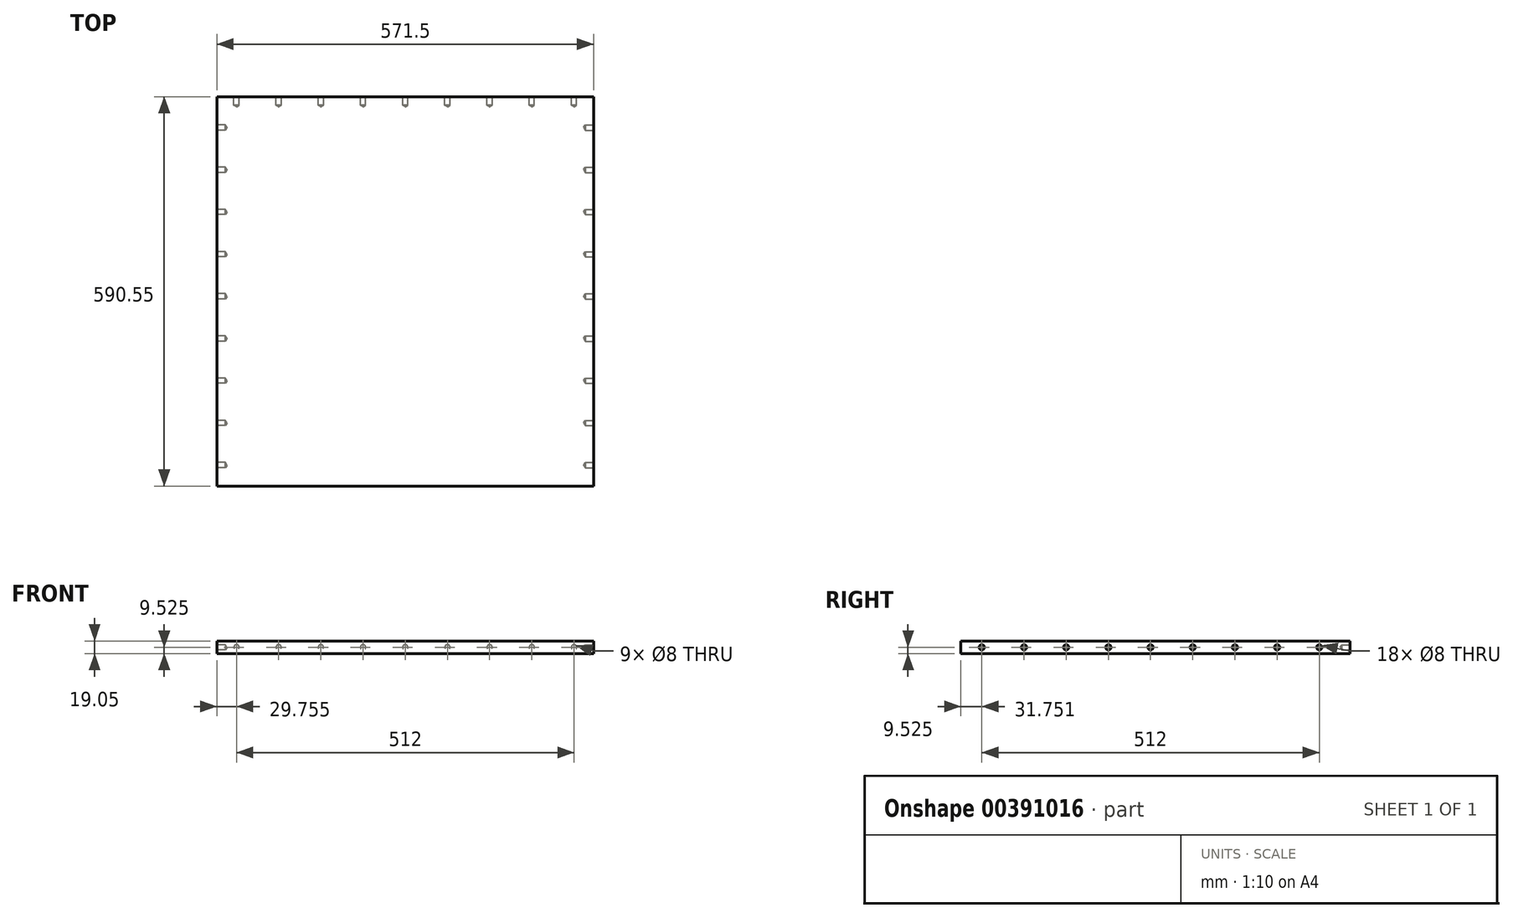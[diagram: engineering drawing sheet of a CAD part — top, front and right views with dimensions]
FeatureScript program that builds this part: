
annotation { "Feature Type Name" : "Feature", "Feature Type Description" : "" }
export const myFeature = defineFeature(function(context is Context, id is Id, definition is map)
    precondition{}
    {
        {
            var Q0;
            Q0=qCreatedBy(makeId("Top.planeOp"),FACE);
            var sketch = newSketch(context, id + "F0", { "sketchPlane" : qUnion([Q0])});
            skLineSegment(sketch, "E0.bottom", {"start": v(-308.17, 303.25) * mm, "end": v(263.33, 303.25) * mm});
            skLineSegment(sketch, "E0.top", {"start": v(-308.17, -287.3) * mm, "end": v(263.33, -287.3) * mm});
            skLineSegment(sketch, "E0.left", {"start": v(-308.17, 303.25) * mm, "end": v(-308.17, -287.3) * mm});
            skLineSegment(sketch, "E0.right", {"start": v(263.33, 303.25) * mm, "end": v(263.33, -287.3) * mm});
            skSolve(sketch);
        }
        {
            var Q0;
            Q0=makeQuery(id+"F0.imprint","IMPRINT",FACE,{"disambiguationData":[TD([[makeQuery(id+"F0.imprint","IMPRINT",EDGE,{"derivedFrom":sQuery(id+"F0.wireOp",EDGE,"E0.bottom")}),-1.0]])]});
            extrude(context, id + "F1", {"entities" : qUnion([Q0]), "depth" : 19.05 * mm});
        }
        {
            var Q0;
            Q0=makeQuery(id+"F1.opExtrude","SWEPT_FACE",FACE,{"disambiguationData":[OSD([sQuery(id+"F0.wireOp",EDGE,"E0.right")])]});
            var sketch = newSketch(context, id + "F2", { "sketchPlane" : qUnion([Q0])});
            skCircle(sketch, "E1", {"center": v(-255.55, 9.53) * mm, "radius": 4 * mm});
            skCircle(sketch, "E2.1.0.0", {"center": v(-191.55, 9.53) * mm, "radius": 4 * mm});
            skCircle(sketch, "E2.2.0.0", {"center": v(-127.55, 9.53) * mm, "radius": 4 * mm});
            skCircle(sketch, "E2.3.0.0", {"center": v(-63.55, 9.53) * mm, "radius": 4 * mm});
            skCircle(sketch, "E2.4.0.0", {"center": v(0.45, 9.53) * mm, "radius": 4 * mm});
            skCircle(sketch, "E2.5.0.0", {"center": v(64.45, 9.53) * mm, "radius": 4 * mm});
            skCircle(sketch, "E2.6.0.0", {"center": v(128.45, 9.53) * mm, "radius": 4 * mm});
            skCircle(sketch, "E2.7.0.0", {"center": v(192.45, 9.53) * mm, "radius": 4 * mm});
            skCircle(sketch, "E2.8.0.0", {"center": v(256.45, 9.53) * mm, "radius": 4 * mm});
            skLineSegment(sketch, "E2.direction1", {"start": v(-255.55, 9.53) * mm, "end": v(-191.55, 9.53) * mm, "construction": true});
            skSolve(sketch);
        }
        {
            var Q0;
            Q0=sQuery(id+"F2.wireOp",VERTEX,"E2.direction1.start");
            var Q1;
            Q1=sQuery(id+"F2.wireOp",VERTEX,"E2.1.0.0.center");
            var Q2;
            Q2=sQuery(id+"F2.wireOp",VERTEX,"E2.2.0.0.center");
            var Q3;
            Q3=sQuery(id+"F2.wireOp",VERTEX,"E2.3.0.0.center");
            var Q4;
            Q4=sQuery(id+"F2.wireOp",VERTEX,"E2.4.0.0.center");
            var Q5;
            Q5=sQuery(id+"F2.wireOp",VERTEX,"E2.5.0.0.center");
            var Q6;
            Q6=sQuery(id+"F2.wireOp",VERTEX,"E2.6.0.0.center");
            var Q7;
            Q7=sQuery(id+"F2.wireOp",VERTEX,"E2.7.0.0.center");
            var Q8;
            Q8=sQuery(id+"F2.wireOp",VERTEX,"E2.8.0.0.center");
            var Q9;
            Q9=makeQuery(id+"F1.opExtrude","SWEPT_BODY",BODY,{"disambiguationData":[OSD([sQuery(id+"F0.wireOp",EDGE,"E0.bottom"),sQuery(id+"F0.wireOp",EDGE,"E0.top"),sQuery(id+"F0.wireOp",EDGE,"E0.left"),sQuery(id+"F0.wireOp",EDGE,"E0.right")])]});
            hole(context, id + "F3", {"style" : HoleStyle.SIMPLE, "endStyle" : HoleEndStyle.BLIND, "standardTappedOrClearance" : lookupTablePath({ "standard" : "ISO", "size" : "8", "type" : "Drilled" }), "standardBlindInLast" : lookupTablePath({ "standard" : "ISO", "size" : "8", "type" : "Drilled" }), "holeDiameter" : 8 * mm, "holeDepth" : 12.7 * mm, "isTappedThrough" : true, "tappedDepth" : 12.7 * mm, "tapClearance" : 3, "startFromSketch" : true, "locations" : qUnion([Q0, Q1, Q2, Q3, Q4, Q5, Q6, Q7, Q8]), "scope" : qUnion([Q9])});
        }
        {
            var Q0;
            Q0=makeQuery(id+"F1.opExtrude","SWEPT_FACE",FACE,{"disambiguationData":[OSD([sQuery(id+"F0.wireOp",EDGE,"E0.left")])]});
            var sketch = newSketch(context, id + "F4", { "sketchPlane" : qUnion([Q0])});
            skCircle(sketch, "E3", {"center": v(255.55, 9.53) * mm, "radius": 4 * mm});
            skCircle(sketch, "E4.1.0.0", {"center": v(191.55, 9.53) * mm, "radius": 4 * mm});
            skCircle(sketch, "E4.2.0.0", {"center": v(127.55, 9.53) * mm, "radius": 4 * mm});
            skCircle(sketch, "E4.3.0.0", {"center": v(63.55, 9.53) * mm, "radius": 4 * mm});
            skCircle(sketch, "E4.4.0.0", {"center": v(-0.45, 9.53) * mm, "radius": 4 * mm});
            skCircle(sketch, "E4.5.0.0", {"center": v(-64.45, 9.53) * mm, "radius": 4 * mm});
            skCircle(sketch, "E4.6.0.0", {"center": v(-128.45, 9.53) * mm, "radius": 4 * mm});
            skCircle(sketch, "E4.7.0.0", {"center": v(-192.45, 9.53) * mm, "radius": 4 * mm});
            skCircle(sketch, "E4.8.0.0", {"center": v(-256.45, 9.53) * mm, "radius": 4 * mm});
            skLineSegment(sketch, "E4.direction1", {"start": v(255.55, 9.53) * mm, "end": v(191.55, 9.53) * mm, "construction": true});
            skSolve(sketch);
        }
        {
            var Q0;
            Q0=sQuery(id+"F4.wireOp",VERTEX,"E3.center");
            var Q1;
            Q1=sQuery(id+"F4.wireOp",VERTEX,"E4.direction1.end");
            var Q2;
            Q2=sQuery(id+"F4.wireOp",VERTEX,"E4.2.0.0.center");
            var Q3;
            Q3=sQuery(id+"F4.wireOp",VERTEX,"E4.3.0.0.center");
            var Q4;
            Q4=sQuery(id+"F4.wireOp",VERTEX,"E4.5.0.0.center");
            var Q5;
            Q5=sQuery(id+"F4.wireOp",VERTEX,"E4.4.0.0.center");
            var Q6;
            Q6=sQuery(id+"F4.wireOp",VERTEX,"E4.6.0.0.center");
            var Q7;
            Q7=sQuery(id+"F4.wireOp",VERTEX,"E4.7.0.0.center");
            var Q8;
            Q8=sQuery(id+"F4.wireOp",VERTEX,"E4.8.0.0.center");
            var Q9;
            Q9=makeQuery(id+"F1.opExtrude","SWEPT_BODY",BODY,{"disambiguationData":[OSD([sQuery(id+"F0.wireOp",EDGE,"E0.bottom"),sQuery(id+"F0.wireOp",EDGE,"E0.top"),sQuery(id+"F0.wireOp",EDGE,"E0.left"),sQuery(id+"F0.wireOp",EDGE,"E0.right")])]});
            hole(context, id + "F5", {"style" : HoleStyle.SIMPLE, "endStyle" : HoleEndStyle.BLIND, "standardTappedOrClearance" : lookupTablePath({ "standard" : "ISO", "size" : "8", "type" : "Drilled" }), "standardBlindInLast" : lookupTablePath({ "standard" : "ISO", "size" : "8", "type" : "Drilled" }), "holeDiameter" : 8 * mm, "holeDepth" : 12.7 * mm, "isTappedThrough" : true, "tappedDepth" : 12.7 * mm, "tapClearance" : 3, "startFromSketch" : true, "locations" : qUnion([Q0, Q1, Q2, Q3, Q4, Q5, Q6, Q7, Q8]), "scope" : qUnion([Q9])});
        }
        {
            var Q0;
            Q0=makeQuery(id+"F1.opExtrude","SWEPT_FACE",FACE,{"disambiguationData":[OSD([sQuery(id+"F0.wireOp",EDGE,"E0.bottom")])]});
            var sketch = newSketch(context, id + "F6", { "sketchPlane" : qUnion([Q0])});
            skCircle(sketch, "E5", {"center": v(-233.59, 9.52) * mm, "radius": 4 * mm});
            skCircle(sketch, "E6.1.0.0", {"center": v(-169.59, 9.53) * mm, "radius": 4 * mm});
            skCircle(sketch, "E6.2.0.0", {"center": v(-105.59, 9.52) * mm, "radius": 4 * mm});
            skCircle(sketch, "E6.3.0.0", {"center": v(-41.59, 9.52) * mm, "radius": 4 * mm});
            skCircle(sketch, "E6.4.0.0", {"center": v(22.41, 9.52) * mm, "radius": 4 * mm});
            skCircle(sketch, "E6.5.0.0", {"center": v(86.41, 9.52) * mm, "radius": 4 * mm});
            skCircle(sketch, "E6.6.0.0", {"center": v(150.41, 9.52) * mm, "radius": 4 * mm});
            skCircle(sketch, "E6.7.0.0", {"center": v(214.41, 9.52) * mm, "radius": 4 * mm});
            skCircle(sketch, "E6.8.0.0", {"center": v(278.41, 9.52) * mm, "radius": 4 * mm});
            skLineSegment(sketch, "E6.direction1", {"start": v(-233.59, 9.52) * mm, "end": v(-169.59, 9.52) * mm, "construction": true});
            skSolve(sketch);
        }
        {
            var Q0;
            Q0 = qSketchRegion(id + "F6", true);
            extrude(context, id + "F7", {"entities" : qUnion([Q0]), "operationType" : NewBodyOperationType.ADD, "oppositeDirection" : true, "depth" : 12.7 * mm});
        }
        {
            var Q0;
            Q0=sQuery(id+"F6.wireOp",VERTEX,"E6.direction1.start");
            var Q1;
            Q1=sQuery(id+"F6.wireOp",VERTEX,"E6.1.0.0.center");
            var Q2;
            Q2=sQuery(id+"F6.wireOp",VERTEX,"E6.2.0.0.center");
            var Q3;
            Q3=sQuery(id+"F6.wireOp",VERTEX,"E6.3.0.0.center");
            var Q4;
            Q4=sQuery(id+"F6.wireOp",VERTEX,"E6.4.0.0.center");
            var Q5;
            Q5=sQuery(id+"F6.wireOp",VERTEX,"E6.5.0.0.center");
            var Q6;
            Q6=sQuery(id+"F6.wireOp",VERTEX,"E6.6.0.0.center");
            var Q7;
            Q7=sQuery(id+"F6.wireOp",VERTEX,"E6.7.0.0.center");
            var Q8;
            Q8=sQuery(id+"F6.wireOp",VERTEX,"E6.8.0.0.center");
            var Q9;
            Q9=makeQuery(id+"F1.opExtrude","SWEPT_BODY",BODY,{"disambiguationData":[OSD([sQuery(id+"F0.wireOp",EDGE,"E0.bottom"),sQuery(id+"F0.wireOp",EDGE,"E0.top"),sQuery(id+"F0.wireOp",EDGE,"E0.left"),sQuery(id+"F0.wireOp",EDGE,"E0.right")])]});
            hole(context, id + "F8", {"style" : HoleStyle.SIMPLE, "endStyle" : HoleEndStyle.BLIND, "standardTappedOrClearance" : lookupTablePath({ "standard" : "ISO", "size" : "8", "type" : "Drilled" }), "standardBlindInLast" : lookupTablePath({ "standard" : "ISO", "size" : "8", "type" : "Drilled" }), "holeDiameter" : 8 * mm, "holeDepth" : 12.7 * mm, "isTappedThrough" : true, "tappedDepth" : 12.7 * mm, "tapClearance" : 3, "startFromSketch" : true, "locations" : qUnion([Q0, Q1, Q2, Q3, Q4, Q5, Q6, Q7, Q8]), "scope" : qUnion([Q9])});
        }
    });
